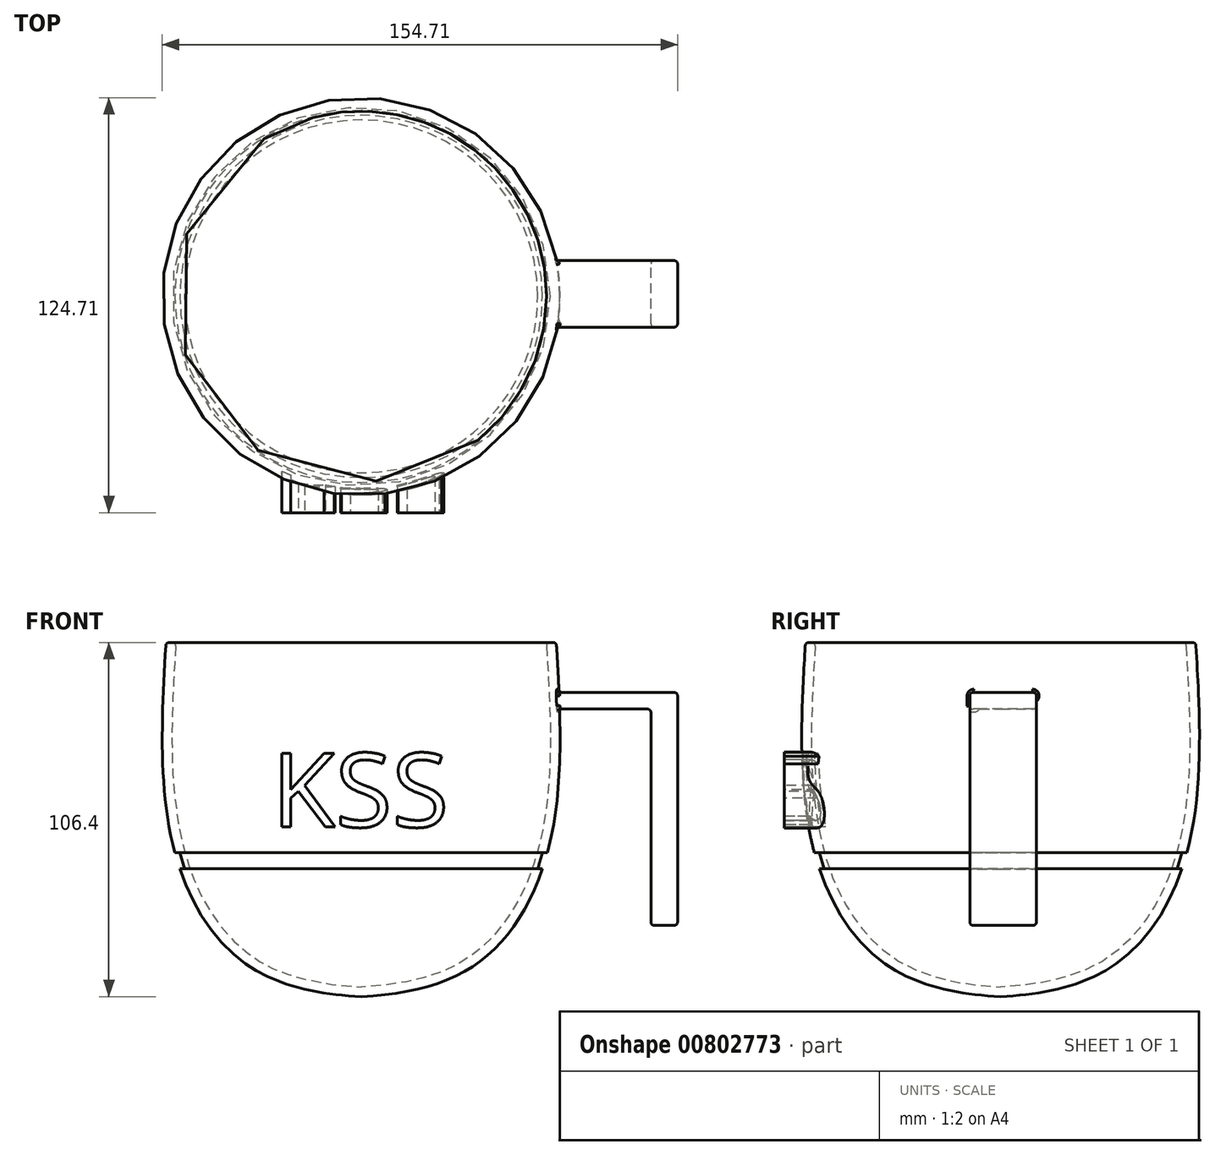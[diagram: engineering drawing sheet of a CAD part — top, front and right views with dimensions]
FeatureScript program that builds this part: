
annotation { "Feature Type Name" : "Feature", "Feature Type Description" : "" }
export const myFeature = defineFeature(function(context is Context, id is Id, definition is map)
    precondition{}
    {
        {
            var Q0;
            Q0=qCreatedBy(makeId("Front.planeOp"),FACE);
            var sketch = newSketch(context, id + "F0", { "sketchPlane" : qUnion([Q0])});
            skFitSpline(sketch, "E0", {"points": [v(58.2, 49.23) * mm, v(57.8, -11.76) * mm, v(42.66, -46.44) * mm, v(17.54, -61.2) * mm, v(-29.9, -63.58) * mm], "startDerivative": vector(13.8, -216.78) * mm, "endDerivative": vector(-194.84, 4.78) * mm});
            skFitSpline(sketch, "E1.0", {"points": [v(55.2, 49.04) * mm, v(55.5, 44.53) * mm, v(56.07, 35.51) * mm, v(56.68, 22.24) * mm, v(56.79, 9.42) * mm, v(56.26, -0.72) * mm, v(55.35, -8.4) * mm, v(54.4, -13.9) * mm, v(53.17, -19.16) * mm, v(51.16, -25.82) * mm, v(48.63, -31.9) * mm, v(45.64, -37.34) * mm, v(43.16, -41.08) * mm, v(40.48, -44.47) * mm, v(37.6, -47.48) * mm, v(34.51, -50.14) * mm, v(30.07, -53.25) * mm, v(25.12, -55.73) * mm, v(19.55, -57.62) * mm, v(13.54, -59.12) * mm, v(5.17, -60.3) * mm, v(-9.6, -61.08) * mm, v(-21.7, -60.78) * mm, v(-29.83, -60.59) * mm]});
            skLineSegment(sketch, "E2", {"start": v(0, 49.63) * mm, "end": v(0, -68.77) * mm});
            skLineSegment(sketch, "E3", {"start": v(28.3, 42.85) * mm, "end": v(77.34, 42.85) * mm});
            skLineSegment(sketch, "E4.bottom", {"start": v(55.9, -20.31) * mm, "end": v(54.42, -20.31) * mm});
            skLineSegment(sketch, "E5", {"start": v(54.42, -20.31) * mm, "end": v(53.02, -25.24) * mm});
            skLineSegment(sketch, "E6", {"start": v(53.02, -25.24) * mm, "end": v(54.42, -25.18) * mm});
            skSolve(sketch);
        }
        {
            var Q0;
            {var subQ0=sQuery(id+"F0.wireOp",EDGE,"E2");var subQ1=sQuery(id+"F0.wireOp",EDGE,"E0");var subQ2=makeQuery(id+"F0.imprint","INTERSECT",VERTEX,{"derivedFrom":[subQ1,subQ0]});Q0=makeQuery(id+"F0.imprint","IMPRINT",FACE,{"disambiguationData":[TD([[makeQuery(id+"F0.imprint","IMPRINT",EDGE,{"disambiguationData":[TD([[subQ2,1.0]])],"derivedFrom":subQ1}),-1.0]])]});}
            var Q1;
            Q1=sQuery(id+"F0.wireOp",EDGE,"E2");
            revolve(context, id + "F1", {"surfaceOperationType" : NewSurfaceOperationType.NEW, "entities" : qUnion([Q0]), "axis" : qUnion([Q1]), "revolveType" : RevolveType.FULL});
        }
        {
            var Q0;
            Q0=qCreatedBy(makeId("Front.planeOp"),FACE);
            cPlane(context, id + "F2", {"entities" : qUnion([Q0]), "cplaneType" : CPlaneType.OFFSET, "offset" : 65 * mm, "width" : 150 * mm, "height" : 150 * mm});
        }
        {
            var Q0;
            Q0=qCreatedBy(id+"F2.planeOp",FACE);
            var sketch = newSketch(context, id + "F3", { "sketchPlane" : qUnion([Q0])});
            skText(sketch, "E7", { "text": "KSS\n", "fontName": "OpenSans-Regular.ttf"});
            const initialGuessF3  = {"E7": [-0.0268, -0.01256, 1, 0, 0.02232]};
            skSetInitialGuess(sketch, initialGuessF3);
            skSolve(sketch);
        }
        {
            var Q0;
            Q0 = qSketchRegion(id + "F3", true);
            extrude(context, id + "F4", {"entities" : qUnion([Q0]), "operationType" : NewBodyOperationType.ADD, "endBound" : BoundingType.UP_TO_NEXT, "oppositeDirection" : true, "depth" : 25 * mm, "offsetDistance" : 25 * mm});
        }
        {
            var Q0;
            Q0=qCreatedBy(makeId("Right.planeOp"),FACE);
            cPlane(context, id + "F5", {"entities" : qUnion([Q0]), "cplaneType" : CPlaneType.OFFSET, "offset" : 95 * mm, "width" : 150 * mm, "height" : 150 * mm});
        }
        {
            var Q0;
            Q0=qCreatedBy(id+"F5.planeOp",FACE);
            var sketch = newSketch(context, id + "F6", { "sketchPlane" : qUnion([Q0])});
            skLineSegment(sketch, "E8.bottom", {"start": v(-9.24, 27.85) * mm, "end": v(10.76, 27.85) * mm});
            skLineSegment(sketch, "E8.top", {"start": v(-9.24, 22.85) * mm, "end": v(10.76, 22.85) * mm});
            skLineSegment(sketch, "E8.left", {"start": v(-9.24, 27.85) * mm, "end": v(-9.24, 22.85) * mm});
            skLineSegment(sketch, "E8.right", {"start": v(10.76, 27.85) * mm, "end": v(10.76, 22.85) * mm});
            skSolve(sketch);
        }
        {
            var Q0;
            Q0=makeQuery(id+"F6.imprint","IMPRINT",FACE,{"disambiguationData":[TD([[makeQuery(id+"F6.imprint","IMPRINT",EDGE,{"derivedFrom":sQuery(id+"F6.wireOp",EDGE,"E8.bottom")}),-1.0]])]});
            extrude(context, id + "F7", {"entities" : qUnion([Q0]), "operationType" : NewBodyOperationType.ADD, "endBound" : BoundingType.UP_TO_NEXT, "oppositeDirection" : true, "depth" : 25 * mm, "offsetDistance" : 25 * mm});
        }
        {
            var Q0;
            Q0=makeQuery(id+"F7.opExtrude","SWEPT_FACE",FACE,{"disambiguationData":[OSD([sQuery(id+"F6.wireOp",EDGE,"E8.bottom")])]});
            var sketch = newSketch(context, id + "F8", { "sketchPlane" : qUnion([Q0])});
            skLineSegment(sketch, "E9.bottom", {"start": v(87, -9.24) * mm, "end": v(95, -9.24) * mm});
            skLineSegment(sketch, "E9.top", {"start": v(87, 10.76) * mm, "end": v(95, 10.76) * mm});
            skLineSegment(sketch, "E9.left", {"start": v(87, -9.24) * mm, "end": v(87, 10.76) * mm});
            skLineSegment(sketch, "E9.right", {"start": v(95, -9.24) * mm, "end": v(95, 10.76) * mm});
            skSolve(sketch);
        }
        {
            var Q0;
            Q0=makeQuery(id+"F8.imprint","IMPRINT",FACE,{"disambiguationData":[TD([[makeQuery(id+"F8.imprint","IMPRINT",EDGE,{"derivedFrom":sQuery(id+"F8.wireOp",EDGE,"E9.bottom")}),1.0]])]});
            extrude(context, id + "F9", {"entities" : qUnion([Q0]), "operationType" : NewBodyOperationType.ADD, "oppositeDirection" : true, "depth" : 70 * mm, "offsetDistance" : 25 * mm});
        }
        {
            var Q0;
            Q0=makeQuery(id+"F7.opExtrude","SWEPT_FACE",FACE,{"disambiguationData":[OSD([sQuery(id+"F6.wireOp",EDGE,"E8.bottom")])]});
            var Q1;
            Q1=makeQuery(id+"F9.boolean.opBoolean","MERGE",FACE,{"derivedFrom":[makeQuery(id+"F7.opExtrude","CAP_FACE",FACE,{"disambiguationData":[OSD([sQuery(id+"F6.wireOp",EDGE,"E8.bottom"),sQuery(id+"F6.wireOp",EDGE,"E8.top"),sQuery(id+"F6.wireOp",EDGE,"E8.left"),sQuery(id+"F6.wireOp",EDGE,"E8.right")])],"isStart":true}),makeQuery(id+"F9.opExtrude","SWEPT_FACE",FACE,{"disambiguationData":[OSD([sQuery(id+"F8.wireOp",EDGE,"E9.right")])]})]});
            var Q2;
            Q2=makeQuery(id+"F9.boolean.opBoolean","MERGE",EDGE,{"derivedFrom":[makeQuery(id+"F7.opExtrude","CAP_EDGE",EDGE,{"disambiguationData":[OSD([sQuery(id+"F6.wireOp",EDGE,"E8.right")])],"isStart":true}),makeQuery(id+"F9.opExtrude","SWEPT_EDGE",EDGE,{"disambiguationData":[OSD([sQuery(id+"F8.wireOp",EDGE,"E9.top"),sQuery(id+"F8.wireOp",EDGE,"E9.right")])]})]});
            var Q3;
            Q3=makeQuery(id+"F9.opExtrude","SWEPT_EDGE",EDGE,{"disambiguationData":[OSD([sQuery(id+"F6.wireOp",EDGE,"E8.bottom"),sQuery(id+"F6.wireOp",EDGE,"E8.right"),sQuery(id+"F8.wireOp",EDGE,"E9.top"),sQuery(id+"F8.wireOp",EDGE,"E9.left")])]});
            var Q4;
            Q4=makeQuery(id+"F9.opExtrude","SWEPT_FACE",FACE,{"disambiguationData":[OSD([sQuery(id+"F8.wireOp",EDGE,"E9.left")])]});
            var Q5;
            Q5=makeQuery(id+"F9.boolean.opBoolean","MERGE",FACE,{"derivedFrom":[makeQuery(id+"F7.opExtrude","SWEPT_FACE",FACE,{"disambiguationData":[OSD([sQuery(id+"F6.wireOp",EDGE,"E8.left")])]}),makeQuery(id+"F9.opExtrude","SWEPT_FACE",FACE,{"disambiguationData":[OSD([sQuery(id+"F8.wireOp",EDGE,"E9.bottom")])]})]});
            var Q6;
            Q6=makeQuery(id+"F9.opExtrude","CAP_FACE",FACE,{"disambiguationData":[OSD([sQuery(id+"F8.wireOp",EDGE,"E9.bottom"),sQuery(id+"F8.wireOp",EDGE,"E9.top"),sQuery(id+"F8.wireOp",EDGE,"E9.left"),sQuery(id+"F8.wireOp",EDGE,"E9.right")])],"isStart":false});
            var Q7;
            Q7=makeQuery(id+"F7.opExtrude","SWEPT_EDGE",EDGE,{"disambiguationData":[OSD([sQuery(id+"F6.wireOp",EDGE,"E8.top"),sQuery(id+"F6.wireOp",EDGE,"E8.right")])]});
            var Q8;
            Q8=makeQuery(id+"F7.opExtrude","TWEAK_EDGE",EDGE,{"derivedFrom":[makeQuery(id+"F1.opRevolve","SWEPT_FACE",FACE,{"disambiguationData":[OSD([sQuery(id+"F0.wireOp",EDGE,"E0")])]}),makeQuery(id+"F6.imprint","IMPRINT",EDGE,{"derivedFrom":sQuery(id+"F6.wireOp",EDGE,"E8.top")})]});
            var Q9;
            Q9=makeQuery(id+"F1.opRevolve","SWEPT_EDGE",EDGE,{"disambiguationData":[OSD([sQuery(id+"F0.wireOp",EDGE,"E1.0"),sQuery(id+"F0.wireOp",EDGE,"E3")])]});
            var Q10;
            Q10=makeQuery(id+"F1.opRevolve","SWEPT_EDGE",EDGE,{"disambiguationData":[OSD([sQuery(id+"F0.wireOp",EDGE,"E0"),sQuery(id+"F0.wireOp",EDGE,"E3")])]});
            fillet(context, id + "F10", {"entities" : qUnion([Q0, Q1, Q2, Q3, Q4, Q5, Q6, Q7, Q8, Q9, Q10]), "radius" : 1 * mm, "tangentPropagation" : true, "allowEdgeOverflow" : false});
        }
    });
